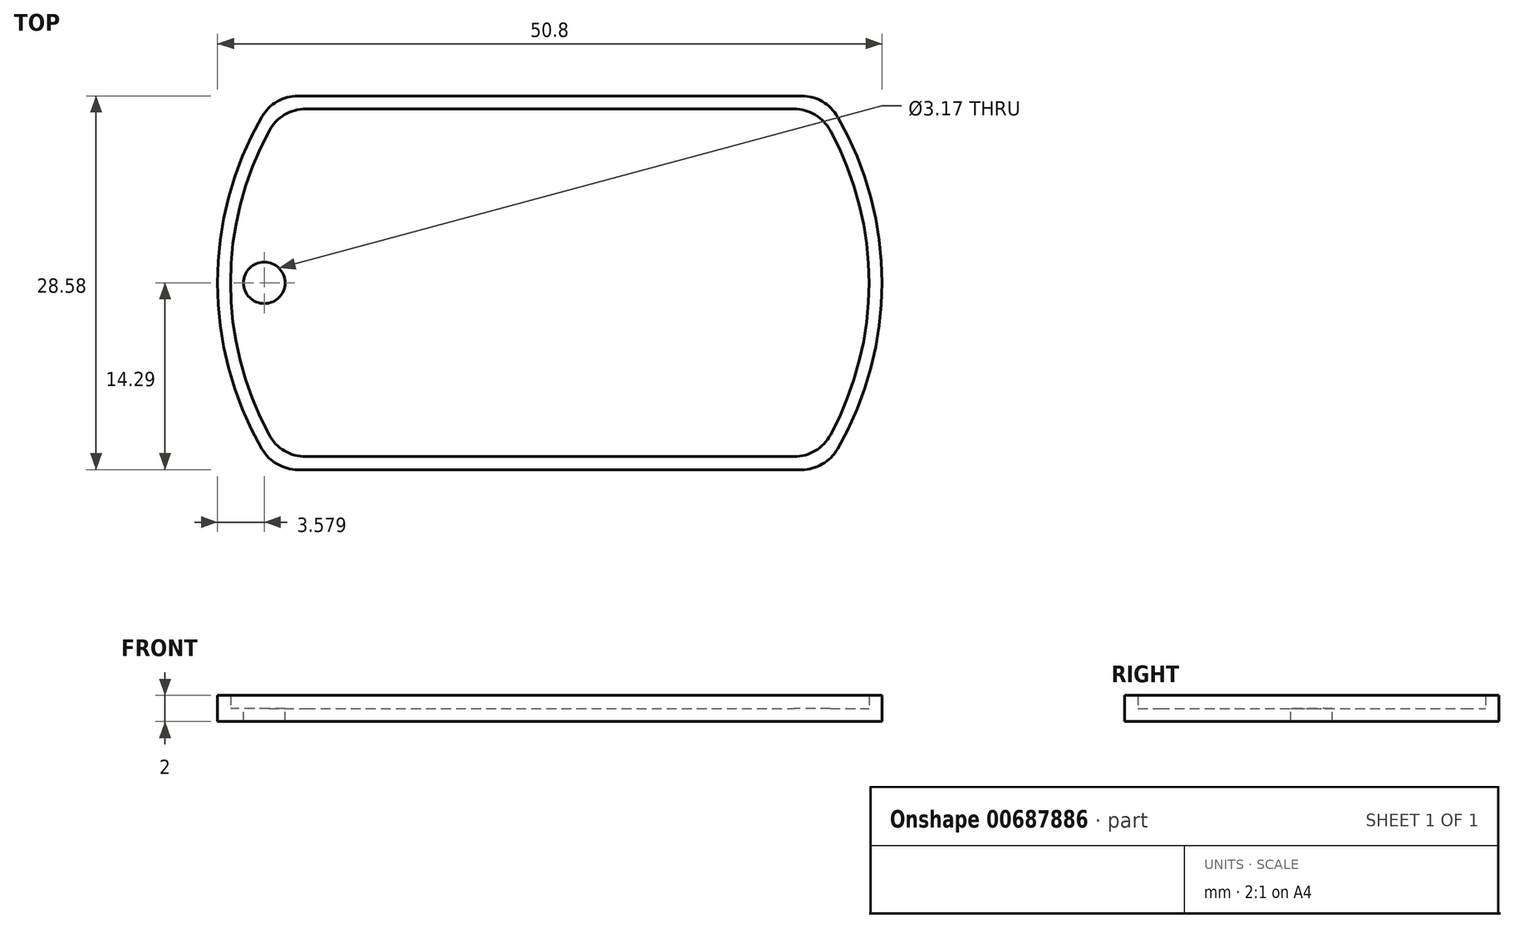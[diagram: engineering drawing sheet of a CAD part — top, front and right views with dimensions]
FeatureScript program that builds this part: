
annotation { "Feature Type Name" : "Feature", "Feature Type Description" : "" }
export const myFeature = defineFeature(function(context is Context, id is Id, definition is map)
    precondition{}
    {
        {
            var Q0;
            Q0=qCreatedBy(makeId("Top.planeOp"),FACE);
            var sketch = newSketch(context, id + "F0", { "sketchPlane" : qUnion([Q0])});
            skArc(sketch, "E0", {"start": v(-22, 12.7) * mm, "mid": v(-25.4, 0) * mm, "end": v(-22, -12.7) * mm});
            skLineSegment(sketch, "E1.top", {"start": v(-19.25, -14.29) * mm, "end": v(19.25, -14.29) * mm});
            skArc(sketch, "E2.trimOffspring", {"start": v(22, -12.7) * mm, "mid": v(25.4, 0) * mm, "end": v(22, 12.7) * mm});
            skLineSegment(sketch, "E3", {"start": v(-19.25, 14.29) * mm, "end": v(19.25, 14.29) * mm});
            skPoint(sketch, "E4.visualSharp", {"position": v(-21, 14.29) * mm});
            skArc(sketch, "E4.filletArc", {"start": v(-19.25, 14.29) * mm, "mid": v(-20.83, 13.86) * mm, "end": v(-22, 12.7) * mm});
            skPoint(sketch, "E5.visualSharp", {"position": v(21, 14.29) * mm});
            skArc(sketch, "E5.filletArc", {"start": v(22, 12.7) * mm, "mid": v(20.83, 13.86) * mm, "end": v(19.25, 14.29) * mm});
            skPoint(sketch, "E6.visualSharp", {"position": v(21, -14.29) * mm});
            skArc(sketch, "E6.filletArc", {"start": v(19.25, -14.29) * mm, "mid": v(20.83, -13.86) * mm, "end": v(22, -12.7) * mm});
            skPoint(sketch, "E7.visualSharp", {"position": v(-21, -14.29) * mm});
            skArc(sketch, "E7.filletArc", {"start": v(-22, -12.7) * mm, "mid": v(-20.83, -13.86) * mm, "end": v(-19.25, -14.29) * mm});
            skSolve(sketch);
        }
        {
            var Q0;
            Q0=makeQuery(id+"F0.imprint","IMPRINT",FACE,{"disambiguationData":[TD([[makeQuery(id+"F0.imprint","IMPRINT",EDGE,{"derivedFrom":sQuery(id+"F0.wireOp",EDGE,"E0")}),1.0]])]});
            extrude(context, id + "F1", {"entities" : qUnion([Q0]), "depth" : 1 * mm, "offsetDistance" : 25.4 * mm});
        }
        {
            var Q0;
            Q0=makeQuery(id+"F1.opExtrude","CAP_FACE",FACE,{"disambiguationData":[OSD([sQuery(id+"F0.wireOp",EDGE,"E0"),sQuery(id+"F0.wireOp",EDGE,"E1.top"),sQuery(id+"F0.wireOp",EDGE,"E2.trimOffspring"),sQuery(id+"F0.wireOp",EDGE,"E3"),sQuery(id+"F0.wireOp",EDGE,"E4.filletArc"),sQuery(id+"F0.wireOp",EDGE,"E5.filletArc"),sQuery(id+"F0.wireOp",EDGE,"E6.filletArc"),sQuery(id+"F0.wireOp",EDGE,"E7.filletArc")])],"isStart":false});
            var sketch = newSketch(context, id + "F2", { "sketchPlane" : qUnion([Q0])});
            skLineSegment(sketch, "E8.0", {"start": v(-18.66, 13.29) * mm, "end": v(18.66, 13.29) * mm});
            skArc(sketch, "E8.1", {"start": v(-21.45, 11.63) * mm, "mid": v(-24.4, 0) * mm, "end": v(-21.45, -11.63) * mm});
            skLineSegment(sketch, "E8.2", {"start": v(-18.66, -13.29) * mm, "end": v(18.66, -13.29) * mm});
            skArc(sketch, "E8.3", {"start": v(21.45, -11.63) * mm, "mid": v(24.4, 0) * mm, "end": v(21.45, 11.63) * mm});
            skPoint(sketch, "E9.visualSharp", {"position": v(-20.46, 13.29) * mm});
            skArc(sketch, "E9.filletArc", {"start": v(-18.66, 13.29) * mm, "mid": v(-20.29, 12.84) * mm, "end": v(-21.45, 11.63) * mm});
            skPoint(sketch, "E10.visualSharp", {"position": v(20.46, 13.29) * mm});
            skArc(sketch, "E10.filletArc", {"start": v(21.45, 11.63) * mm, "mid": v(20.29, 12.84) * mm, "end": v(18.66, 13.29) * mm});
            skPoint(sketch, "E11.visualSharp", {"position": v(20.46, -13.29) * mm});
            skArc(sketch, "E11.filletArc", {"start": v(18.66, -13.29) * mm, "mid": v(20.29, -12.84) * mm, "end": v(21.45, -11.63) * mm});
            skPoint(sketch, "E12.visualSharp", {"position": v(-20.46, -13.29) * mm});
            skArc(sketch, "E12.filletArc", {"start": v(-21.45, -11.63) * mm, "mid": v(-20.29, -12.84) * mm, "end": v(-18.66, -13.29) * mm});
            skLineSegment(sketch, "E13.0", {"start": v(-19.25, 14.29) * mm, "end": v(19.25, 14.29) * mm});
            skArc(sketch, "E13.1", {"start": v(-22, 12.7) * mm, "mid": v(-25.4, 0) * mm, "end": v(-22, -12.7) * mm});
            skLineSegment(sketch, "E13.2", {"start": v(-19.25, -14.29) * mm, "end": v(19.25, -14.29) * mm});
            skArc(sketch, "E13.3", {"start": v(22, -12.7) * mm, "mid": v(25.4, 0) * mm, "end": v(22, 12.7) * mm});
            skPoint(sketch, "E14.visualSharp", {"position": v(-21, -14.29) * mm});
            skArc(sketch, "E14.filletArc", {"start": v(-22, -12.7) * mm, "mid": v(-20.83, -13.86) * mm, "end": v(-19.25, -14.29) * mm});
            skPoint(sketch, "E15.visualSharp", {"position": v(21, -14.29) * mm});
            skArc(sketch, "E15.filletArc", {"start": v(19.25, -14.29) * mm, "mid": v(20.83, -13.86) * mm, "end": v(22, -12.7) * mm});
            skPoint(sketch, "E16.visualSharp", {"position": v(21, 14.29) * mm});
            skArc(sketch, "E16.filletArc", {"start": v(22, 12.7) * mm, "mid": v(20.83, 13.86) * mm, "end": v(19.25, 14.29) * mm});
            skPoint(sketch, "E17.visualSharp", {"position": v(-21, 14.29) * mm});
            skArc(sketch, "E17.filletArc", {"start": v(-19.25, 14.29) * mm, "mid": v(-20.83, 13.86) * mm, "end": v(-22, 12.7) * mm});
            skSolve(sketch);
        }
        {
            var Q0;
            Q0=makeQuery(id+"F2.imprint","IMPRINT",FACE,{"disambiguationData":[TD([[makeQuery(id+"F2.imprint","IMPRINT",EDGE,{"derivedFrom":sQuery(id+"F2.wireOp",EDGE,"E8.0")}),1.0]])]});
            extrude(context, id + "F3", {"entities" : qUnion([Q0]), "operationType" : NewBodyOperationType.ADD, "depth" : 1 * mm, "offsetDistance" : 25.4 * mm});
        }
        {
            var Q0;
            Q0=makeQuery(id+"F1.opExtrude","CAP_FACE",FACE,{"disambiguationData":[OSD([sQuery(id+"F0.wireOp",EDGE,"E0"),sQuery(id+"F0.wireOp",EDGE,"E1.top"),sQuery(id+"F0.wireOp",EDGE,"E2.trimOffspring"),sQuery(id+"F0.wireOp",EDGE,"E3"),sQuery(id+"F0.wireOp",EDGE,"E4.filletArc"),sQuery(id+"F0.wireOp",EDGE,"E5.filletArc"),sQuery(id+"F0.wireOp",EDGE,"E6.filletArc"),sQuery(id+"F0.wireOp",EDGE,"E7.filletArc")])],"isStart":false});
            var sketch = newSketch(context, id + "F4", { "sketchPlane" : qUnion([Q0])});
            skCircle(sketch, "E18", {"center": v(-21.82, 0) * mm, "radius": 1.59 * mm});
            skSolve(sketch);
        }
        {
            var Q0;
            Q0=makeQuery(id+"F4.imprint","IMPRINT",FACE,{"disambiguationData":[TD([[makeQuery(id+"F4.imprint","IMPRINT",EDGE,{"derivedFrom":sQuery(id+"F4.wireOp",EDGE,"E18")}),1.0]])]});
            extrude(context, id + "F5", {"entities" : qUnion([Q0]), "operationType" : NewBodyOperationType.REMOVE, "oppositeDirection" : true, "depth" : 1 * mm, "offsetDistance" : 25.4 * mm});
        }
    });
